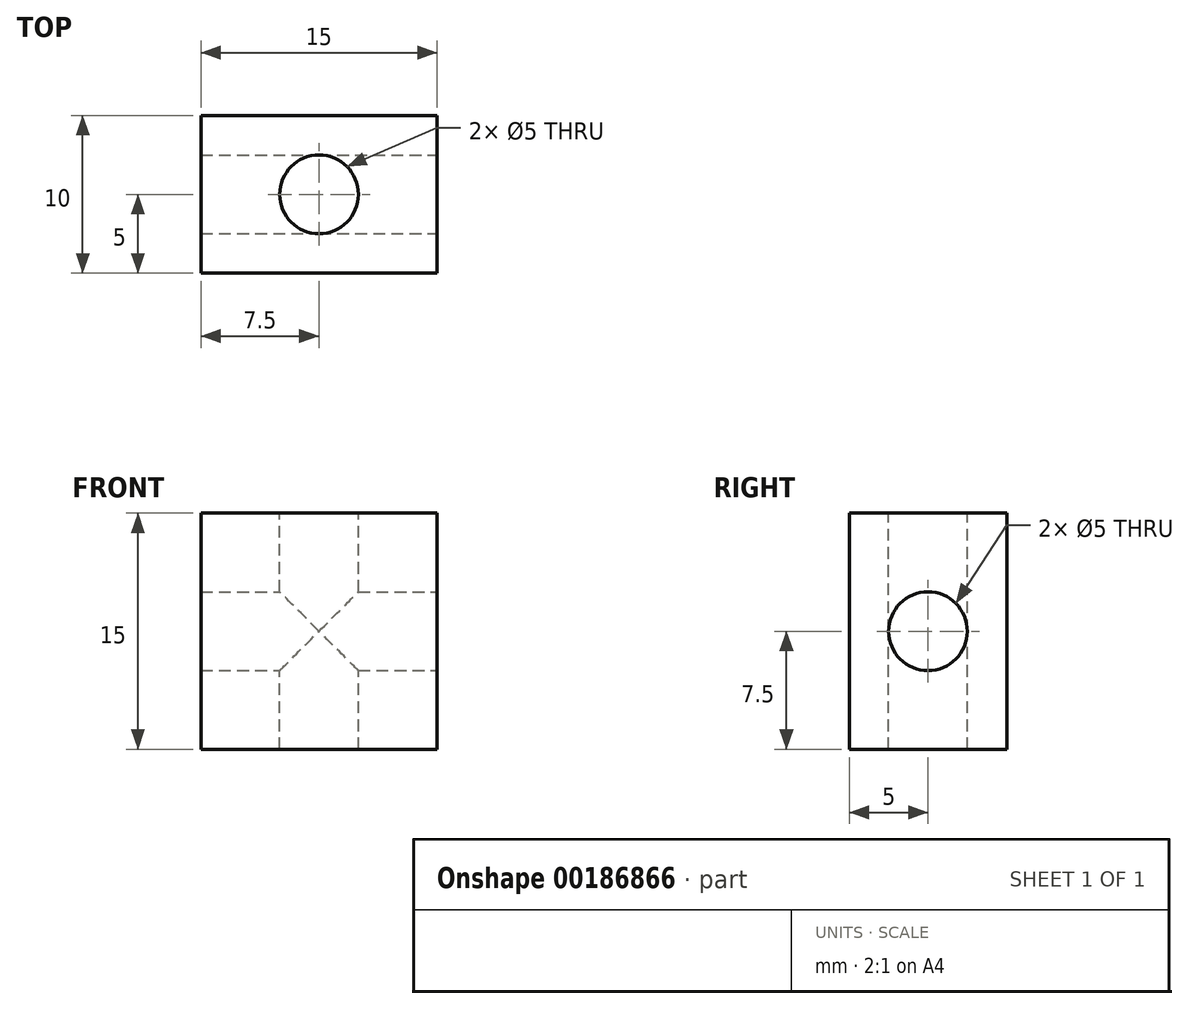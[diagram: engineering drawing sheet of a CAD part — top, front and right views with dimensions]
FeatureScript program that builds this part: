
annotation { "Feature Type Name" : "Feature", "Feature Type Description" : "" }
export const myFeature = defineFeature(function(context is Context, id is Id, definition is map)
    precondition{}
    {
        {
            var Q0;
            Q0=qCreatedBy(makeId("Front.planeOp"),FACE);
            var sketch = newSketch(context, id + "F0", { "sketchPlane" : qUnion([Q0])});
            skLineSegment(sketch, "E0.bottom", {"start": v(7.5, 7.5) * mm, "end": v(-7.5, 7.5) * mm});
            skLineSegment(sketch, "E0.top", {"start": v(7.5, -7.5) * mm, "end": v(-7.5, -7.5) * mm});
            skLineSegment(sketch, "E0.left", {"start": v(7.5, 7.5) * mm, "end": v(7.5, -7.5) * mm});
            skLineSegment(sketch, "E0.right", {"start": v(-7.5, 7.5) * mm, "end": v(-7.5, -7.5) * mm});
            skPoint(sketch, "E0.middle", {"position": v(0, 0) * mm});
            skSolve(sketch);
        }
        {
            var Q0;
            Q0 = qSketchRegion(id + "F0", true);
            extrude(context, id + "F1", {"entities" : qUnion([Q0]), "endBound" : BoundingType.SYMMETRIC, "depth" : 10 * mm});
        }
        {
            var Q0;
            Q0=makeQuery(id+"F1.opExtrude","SWEPT_FACE",FACE,{"disambiguationData":[OSD([sQuery(id+"F0.wireOp",EDGE,"E0.left")])]});
            var sketch = newSketch(context, id + "F2", { "sketchPlane" : qUnion([Q0])});
            skCircle(sketch, "E1", {"center": v(0, 0) * mm, "radius": 2.5 * mm});
            skSolve(sketch);
        }
        {
            var Q0;
            Q0 = qSketchRegion(id + "F2", true);
            extrude(context, id + "F3", {"entities" : qUnion([Q0]), "operationType" : NewBodyOperationType.REMOVE, "endBound" : BoundingType.UP_TO_NEXT, "oppositeDirection" : true, "depth" : 25 * mm});
        }
        {
            var Q0;
            Q0=makeQuery(id+"F1.opExtrude","SWEPT_FACE",FACE,{"disambiguationData":[OSD([sQuery(id+"F0.wireOp",EDGE,"E0.bottom")])]});
            var sketch = newSketch(context, id + "F4", { "sketchPlane" : qUnion([Q0])});
            skCircle(sketch, "E2", {"center": v(0, 0) * mm, "radius": 2.5 * mm});
            skSolve(sketch);
        }
        {
            var Q0;
            Q0 = qSketchRegion(id + "F4", true);
            var Q1;
            Q1=makeQuery(id+"F1.opExtrude","SWEPT_FACE",FACE,{"disambiguationData":[OSD([sQuery(id+"F0.wireOp",EDGE,"E0.top")])]});
            extrude(context, id + "F5", {"entities" : qUnion([Q0]), "operationType" : NewBodyOperationType.REMOVE, "endBound" : BoundingType.UP_TO_SURFACE, "oppositeDirection" : true, "endBoundEntityFace" : qUnion([Q1]), "depth" : 25 * mm});
        }
    });
